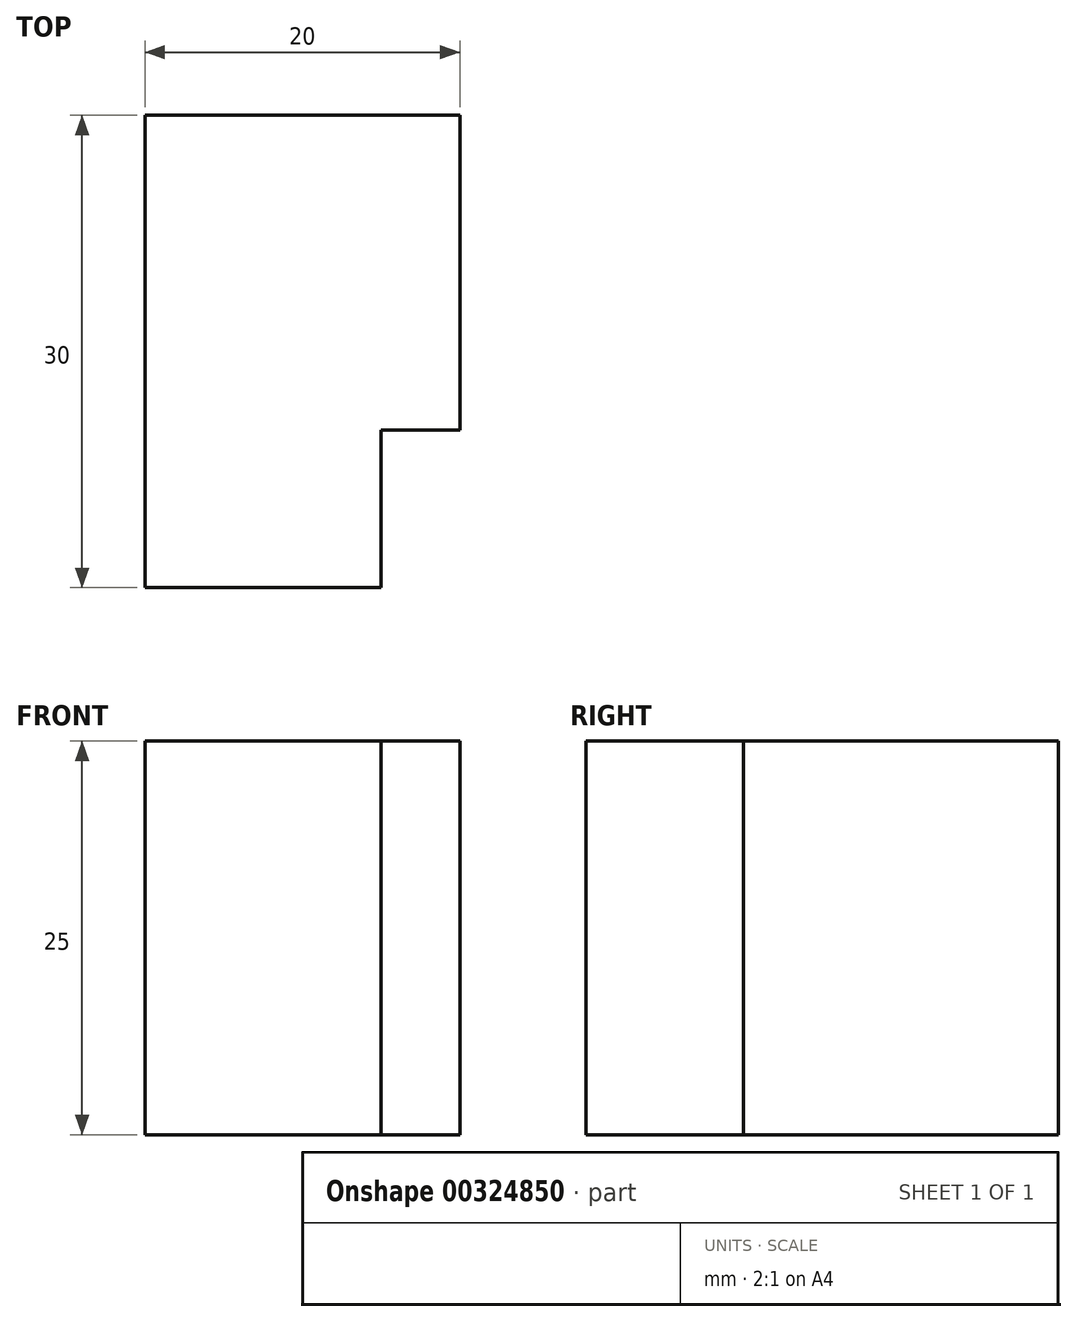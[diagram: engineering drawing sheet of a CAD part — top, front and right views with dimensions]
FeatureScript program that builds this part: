
annotation { "Feature Type Name" : "Feature", "Feature Type Description" : "" }
export const myFeature = defineFeature(function(context is Context, id is Id, definition is map)
    precondition{}
    {
        {
            var Q0;
            Q0=qCreatedBy(makeId("Top.planeOp"),FACE);
            var sketch = newSketch(context, id + "F0", { "sketchPlane" : qUnion([Q0])});
            skLineSegment(sketch, "E0", {"start": v(0, 0) * mm, "end": v(0, 20) * mm});
            skLineSegment(sketch, "E1", {"start": v(0, 20) * mm, "end": v(-20, 20) * mm});
            skLineSegment(sketch, "E2", {"start": v(-20, 20) * mm, "end": v(-20, -10) * mm});
            skLineSegment(sketch, "E3", {"start": v(-20, -10) * mm, "end": v(-5, -10) * mm});
            skLineSegment(sketch, "E4", {"start": v(-5, -10) * mm, "end": v(-5, 0) * mm});
            skLineSegment(sketch, "E5", {"start": v(-5, 0) * mm, "end": v(0, 0) * mm});
            skSolve(sketch);
        }
        {
            var Q0;
            Q0=makeQuery(id+"F0.imprint","IMPRINT",FACE,{"disambiguationData":[TD([[makeQuery(id+"F0.imprint","IMPRINT",EDGE,{"derivedFrom":sQuery(id+"F0.wireOp",EDGE,"E0")}),1.0]])]});
            extrude(context, id + "F1", {"entities" : qUnion([Q0]), "depth" : 25 * mm});
        }
    });
